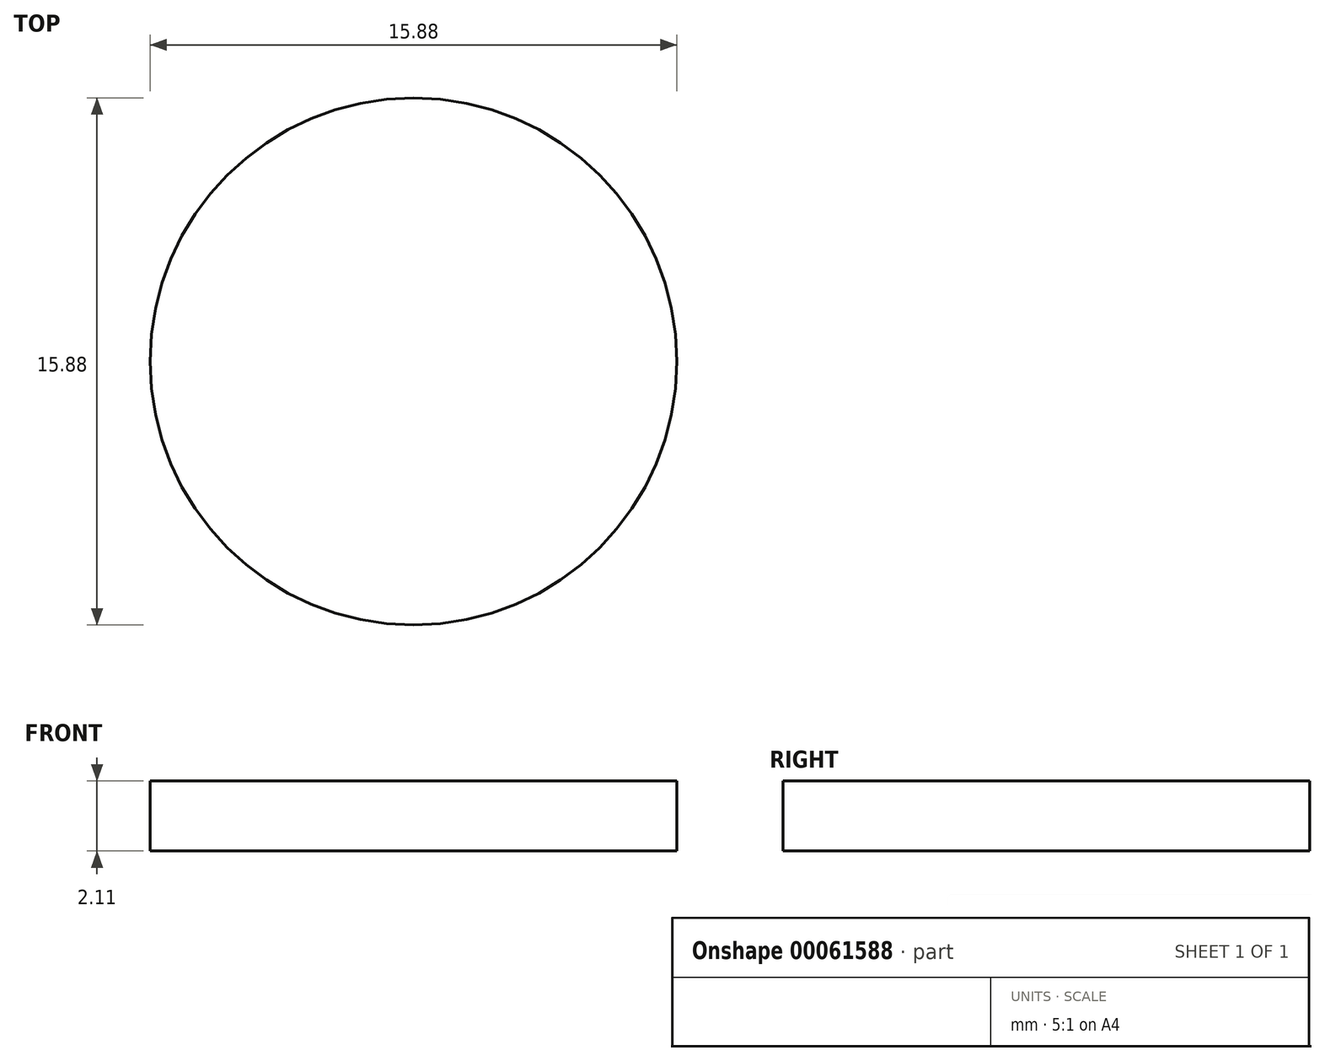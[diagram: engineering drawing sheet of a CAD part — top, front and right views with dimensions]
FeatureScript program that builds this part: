
annotation { "Feature Type Name" : "Feature", "Feature Type Description" : "" }
export const myFeature = defineFeature(function(context is Context, id is Id, definition is map)
    precondition{}
    {
        {
            var Q0;
            Q0=qCreatedBy(makeId("Front.planeOp"),FACE);
            var sketch = newSketch(context, id + "F0", { "sketchPlane" : qUnion([Q0])});
            skLineSegment(sketch, "E0.bottom", {"start": v(-19.05, 19.05) * mm, "end": v(19.05, 19.05) * mm});
            skLineSegment(sketch, "E0.top", {"start": v(-19.05, -19.05) * mm, "end": v(19.05, -19.05) * mm});
            skLineSegment(sketch, "E0.left", {"start": v(-19.05, 19.05) * mm, "end": v(-19.05, -19.05) * mm});
            skLineSegment(sketch, "E0.right", {"start": v(19.05, 19.05) * mm, "end": v(19.05, -19.05) * mm});
            skLineSegment(sketch, "E1.bottom", {"start": v(-16.94, 16.94) * mm, "end": v(16.94, 16.94) * mm});
            skLineSegment(sketch, "E1.top", {"start": v(-16.94, -16.94) * mm, "end": v(16.94, -16.94) * mm});
            skLineSegment(sketch, "E1.left", {"start": v(-16.94, 16.94) * mm, "end": v(-16.94, -16.94) * mm});
            skLineSegment(sketch, "E1.right", {"start": v(16.94, 16.94) * mm, "end": v(16.94, -16.94) * mm});
            skLineSegment(sketch, "E2", {"start": v(-19.05, 19.05) * mm, "end": v(19.05, -19.05) * mm, "construction": true});
            skSolve(sketch);
        }
        {
            var Q0;
            Q0=makeQuery(id+"F0.imprint","IMPRINT",FACE,{"disambiguationData":[TD([[makeQuery(id+"F0.imprint","IMPRINT",EDGE,{"derivedFrom":sQuery(id+"F0.wireOp",EDGE,"E0.bottom")}),-1.0]])]});
            extrude(context, id + "F1", {"entities" : qUnion([Q0]), "endBound" : BoundingType.SYMMETRIC, "depth" : 457.2 * mm});
        }
        {
            var Q0;
            Q0=makeQuery(id+"F1.opExtrude","SWEPT_FACE",FACE,{"disambiguationData":[OSD([sQuery(id+"F0.wireOp",EDGE,"E0.right")])]});
            var sketch = newSketch(context, id + "F2", { "sketchPlane" : qUnion([Q0])});
            skLineSegment(sketch, "E3", {"start": v(-228.6, 19.05) * mm, "end": v(-190.5, -19.05) * mm});
            skLineSegment(sketch, "E4", {"start": v(-190.5, -19.05) * mm, "end": v(-228.6, -19.05) * mm});
            skLineSegment(sketch, "E5", {"start": v(-228.6, -19.05) * mm, "end": v(-228.6, 19.05) * mm});
            skLineSegment(sketch, "E6.MirrorCS", {"start": v(228.6, 19.05) * mm, "end": v(190.5, -19.05) * mm});
            skLineSegment(sketch, "E7.MirrorCS", {"start": v(190.5, -19.05) * mm, "end": v(228.6, -19.05) * mm});
            skLineSegment(sketch, "E8.MirrorCS", {"start": v(228.6, -19.05) * mm, "end": v(228.6, 19.05) * mm});
            skSolve(sketch);
        }
        {
            var Q0;
            Q0=makeQuery(id+"F2.imprint","IMPRINT",FACE,{"disambiguationData":[TD([[makeQuery(id+"F2.imprint","IMPRINT",EDGE,{"derivedFrom":sQuery(id+"F2.wireOp",EDGE,"E3")}),-1.0]])]});
            var Q1;
            Q1=makeQuery(id+"F2.imprint","IMPRINT",FACE,{"disambiguationData":[TD([[makeQuery(id+"F2.imprint","IMPRINT",EDGE,{"derivedFrom":sQuery(id+"F2.wireOp",EDGE,"E6.MirrorCS")}),1.0]])]});
            extrude(context, id + "F3", {"entities" : qUnion([Q0, Q1]), "operationType" : NewBodyOperationType.REMOVE, "endBound" : BoundingType.THROUGH_ALL, "oppositeDirection" : true, "depth" : 25.4 * mm});
        }
        {
            var Q0;
            Q0=makeQuery(id+"F1.opExtrude","SWEPT_FACE",FACE,{"disambiguationData":[OSD([sQuery(id+"F0.wireOp",EDGE,"E0.bottom")])]});
            var sketch = newSketch(context, id + "F4", { "sketchPlane" : qUnion([Q0])});
            skCircle(sketch, "E9", {"center": v(0, 209.55) * mm, "radius": 7.94 * mm});
            skCircle(sketch, "E10.MirrorC", {"center": v(0, -209.55) * mm, "radius": 7.94 * mm});
            skSolve(sketch);
        }
        {
            var Q0;
            Q0=makeQuery(id+"F4.imprint","IMPRINT",FACE,{"disambiguationData":[TD([[makeQuery(id+"F4.imprint","IMPRINT",EDGE,{"derivedFrom":sQuery(id+"F4.wireOp",EDGE,"E9")}),1.0]])]});
            var Q1;
            Q1=makeQuery(id+"F4.imprint","IMPRINT",FACE,{"disambiguationData":[TD([[makeQuery(id+"F4.imprint","IMPRINT",EDGE,{"derivedFrom":sQuery(id+"F4.wireOp",EDGE,"E10.MirrorC")}),-1.0]])]});
            extrude(context, id + "F5", {"entities" : qUnion([Q0, Q1]), "operationType" : NewBodyOperationType.REMOVE, "endBound" : BoundingType.UP_TO_NEXT, "oppositeDirection" : true, "depth" : 25.4 * mm});
        }
    });
